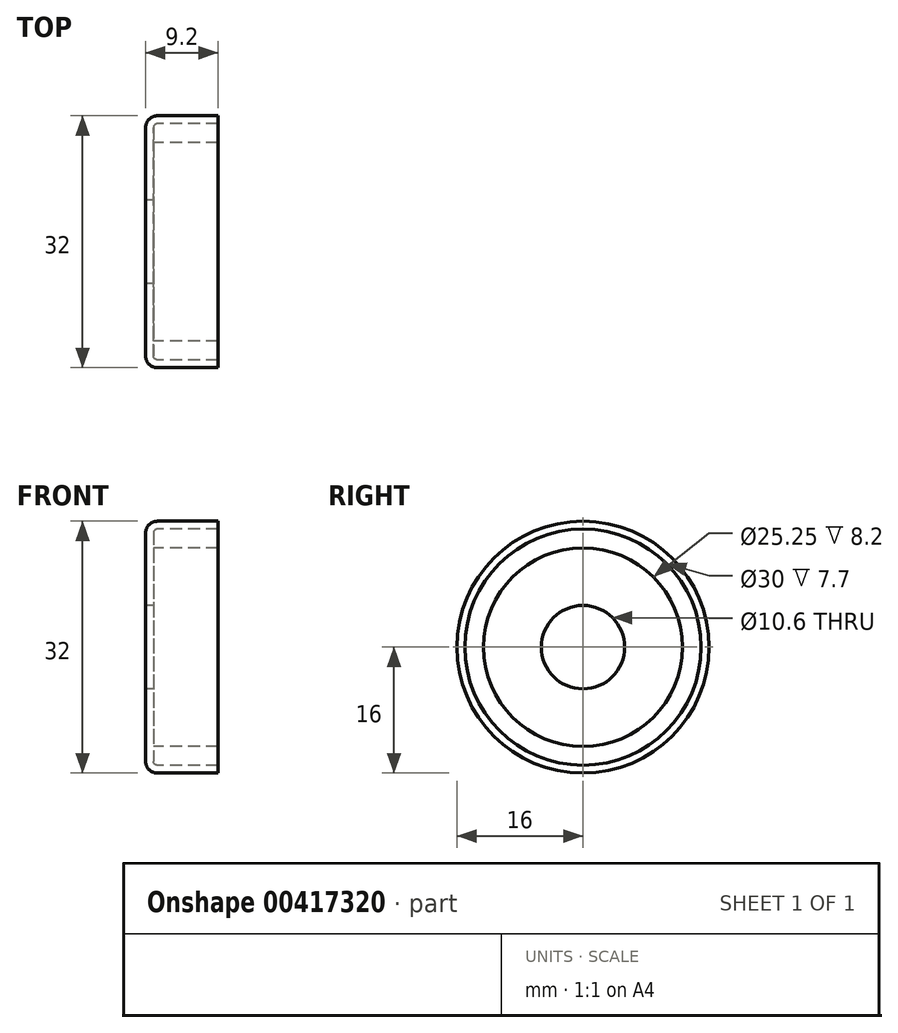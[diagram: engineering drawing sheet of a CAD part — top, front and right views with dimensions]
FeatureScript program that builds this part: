
annotation { "Feature Type Name" : "Feature", "Feature Type Description" : "" }
export const myFeature = defineFeature(function(context is Context, id is Id, definition is map)
    precondition{}
    {
        {
            var Q0;
            Q0=qCreatedBy(makeId("Front.planeOp"),FACE);
            var sketch = newSketch(context, id + "F0", { "sketchPlane" : qUnion([Q0])});
            skLineSegment(sketch, "E0", {"start": v(0, 0) * mm, "end": v(10.1, 0) * mm, "construction": true});
            skLineSegment(sketch, "E1", {"start": v(0, 5.3) * mm, "end": v(0, 14.5) * mm});
            skLineSegment(sketch, "E2", {"start": v(0.5, 15) * mm, "end": v(8.2, 15) * mm});
            skPoint(sketch, "E3.visualSharp", {"position": v(0, 15) * mm});
            skArc(sketch, "E3.filletArc", {"start": v(0.5, 15) * mm, "mid": v(0.15, 14.85) * mm, "end": v(0, 14.5) * mm});
            skLineSegment(sketch, "E4.0", {"start": v(0.5, 16) * mm, "end": v(8.2, 16) * mm});
            skArc(sketch, "E4.1", {"start": v(0.5, 16) * mm, "mid": v(-0.56, 15.56) * mm, "end": v(-1, 14.5) * mm});
            skLineSegment(sketch, "E4.2", {"start": v(-1, 5.3) * mm, "end": v(-1, 14.5) * mm});
            skLineSegment(sketch, "E5", {"start": v(8.2, 16) * mm, "end": v(8.2, 15) * mm});
            skLineSegment(sketch, "E6", {"start": v(-1, 5.3) * mm, "end": v(0, 5.3) * mm});
            skSolve(sketch);
        }
        {
            var Q0;
            Q0 = qSketchRegion(id + "F0", true);
            var Q1;
            Q1=sQuery(id+"F0.wireOp",EDGE,"E0");
            revolve(context, id + "F1", {"entities" : qUnion([Q0]), "axis" : qUnion([Q1]), "revolveType" : RevolveType.FULL});
        }
        {
            var Q0;
            Q0=qCreatedBy(makeId("Front.planeOp"),FACE);
            var sketch = newSketch(context, id + "F2", { "sketchPlane" : qUnion([Q0])});
            skLineSegment(sketch, "E7.0", {"start": v(0, 0) * mm, "end": v(10.1, 0) * mm, "construction": true});
            skLineSegment(sketch, "E8.0", {"start": v(0.5, 15) * mm, "end": v(8.2, 15) * mm});
            skLineSegment(sketch, "E9", {"start": v(8.2, 15) * mm, "end": v(8.2, 12.62) * mm});
            skLineSegment(sketch, "E10", {"start": v(8.2, 12.62) * mm, "end": v(0, 12.62) * mm});
            skPoint(sketch, "E11.orphan", {"position": v(0.5, 15) * mm});
            skArc(sketch, "E12.0", {"start": v(0.5, 15) * mm, "mid": v(0.15, 14.85) * mm, "end": v(0, 14.5) * mm});
            skLineSegment(sketch, "E12.1", {"start": v(0, 12.62) * mm, "end": v(0, 14.5) * mm});
            skPoint(sketch, "E13.orphan", {"position": v(0, 5.3) * mm});
            skSolve(sketch);
        }
        {
            var Q0;
            Q0 = qSketchRegion(id + "F2", true);
            var Q1;
            Q1=sQuery(id+"F2.wireOp",EDGE,"E7.0");
            revolve(context, id + "F3", {"entities" : qUnion([Q0]), "axis" : qUnion([Q1]), "revolveType" : RevolveType.FULL});
        }
    });
